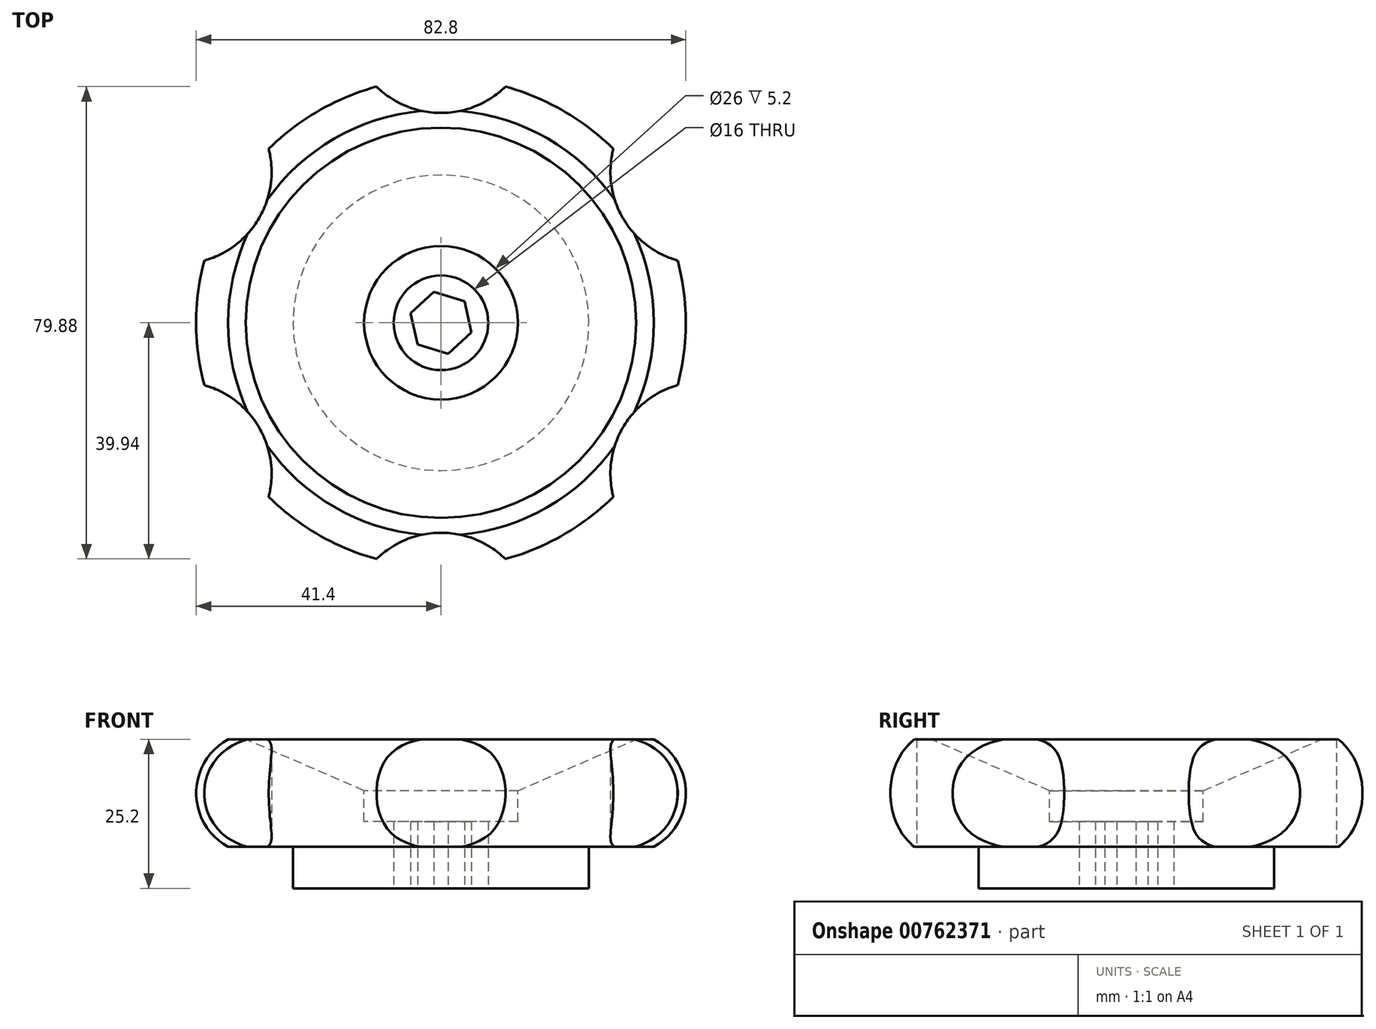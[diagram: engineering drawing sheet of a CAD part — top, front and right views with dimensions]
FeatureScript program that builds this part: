
annotation { "Feature Type Name" : "Feature", "Feature Type Description" : "" }
export const myFeature = defineFeature(function(context is Context, id is Id, definition is map)
    precondition{}
    {
        {
            var Q0;
            Q0=qCreatedBy(makeId("Front.planeOp"),FACE);
            var sketch = newSketch(context, id + "F0", { "sketchPlane" : qUnion([Q0])});
            skLineSegment(sketch, "E0", {"start": v(0, 0) * mm, "end": v(25, 0) * mm});
            skLineSegment(sketch, "E1", {"start": v(25, 0) * mm, "end": v(25, 7) * mm});
            skLineSegment(sketch, "E2", {"start": v(25, 7) * mm, "end": v(36, 7) * mm});
            skLineSegment(sketch, "E3.0", {"start": v(33, 25.2) * mm, "end": v(36, 25.2) * mm});
            skLineSegment(sketch, "E4.0", {"start": v(0, 11.3) * mm, "end": v(13, 11.3) * mm});
            skLineSegment(sketch, "E5", {"start": v(41.4, 60.5) * mm, "end": v(41.4, -63.46) * mm, "construction": true});
            skArc(sketch, "E6", {"start": v(36, 7) * mm, "mid": v(41.4, 16.1) * mm, "end": v(36, 25.2) * mm});
            skLineSegment(sketch, "E7", {"start": v(13, 11.3) * mm, "end": v(13, 16.5) * mm});
            skLineSegment(sketch, "E8", {"start": v(13, 16.5) * mm, "end": v(33, 25.2) * mm});
            skLineSegment(sketch, "E9", {"start": v(0, 11.3) * mm, "end": v(0, 0) * mm});
            skSolve(sketch);
        }
        {
            var Q0;
            Q0=makeQuery(id+"F0.imprint","IMPRINT",FACE,{"disambiguationData":[TD([[makeQuery(id+"F0.imprint","IMPRINT",EDGE,{"derivedFrom":sQuery(id+"F0.wireOp",EDGE,"E0")}),1.0]])]});
            var Q1;
            Q1=sQuery(id+"F0.wireOp",EDGE,"E9");
            revolve(context, id + "F1", {"surfaceOperationType" : NewSurfaceOperationType.NEW, "entities" : qUnion([Q0]), "axis" : qUnion([Q1]), "revolveType" : RevolveType.FULL});
        }
        {
            var Q0;
            Q0=makeQuery(id+"F1.opRevolve","SWEPT_FACE",FACE,{"disambiguationData":[OSD([sQuery(id+"F0.wireOp",EDGE,"E0")])]});
            var sketch = newSketch(context, id + "F2", { "sketchPlane" : qUnion([Q0])});
            skCircle(sketch, "E10", {"center": v(0, 0) * mm, "radius": 8 * mm});
            skLineSegment(sketch, "E11", {"start": v(0, -18.1) * mm, "end": v(0, 35.5) * mm, "construction": true});
            skPoint(sketch, "E12.orphan", {"position": v(-2.52, 3.63) * mm});
            skPoint(sketch, "E13.orphan", {"position": v(2.52, 3.63) * mm});
            skPoint(sketch, "E14.orphan", {"position": v(2.52, 11.78) * mm});
            skPoint(sketch, "E15.orphan", {"position": v(-2.52, 11.78) * mm});
            skLineSegment(sketch, "E16", {"start": v(-10.9, 48.35) * mm, "end": v(-10.9, 28.17) * mm});
            skLineSegment(sketch, "E17.MirrorCS", {"start": v(10.9, 48.35) * mm, "end": v(10.9, 28.17) * mm});
            skCircle(sketch, "E18", {"center": v(0, 0) * mm, "radius": 41.4 * mm, "construction": true});
            skCircle(sketch, "E19", {"center": v(0, 51.1) * mm, "radius": 15.6 * mm});
            skPoint(sketch, "E19.first.point", {"position": v(-10.9, 39.94) * mm});
            skPoint(sketch, "E19.first.point.positionSnap0", {"position": v(-10.9, 38.26) * mm});
            skPoint(sketch, "E19.second.point", {"position": v(10.9, 39.94) * mm});
            skCircle(sketch, "E20.1.0", {"center": v(-44.25, 25.55) * mm, "radius": 15.6 * mm});
            skCircle(sketch, "E20.2.0", {"center": v(-44.25, -25.55) * mm, "radius": 15.6 * mm});
            skCircle(sketch, "E20.3.0", {"center": v(0, -51.1) * mm, "radius": 15.6 * mm});
            skCircle(sketch, "E20.4.0", {"center": v(44.25, -25.55) * mm, "radius": 15.6 * mm});
            skCircle(sketch, "E20.5.0", {"center": v(44.25, 25.55) * mm, "radius": 15.6 * mm});
            skCircle(sketch, "E21.cCircle", {"center": v(0, 0) * mm, "radius": 4.67 * mm, "construction": true});
            skLineSegment(sketch, "E21.0", {"start": v(1.18, 5.26) * mm, "end": v(5.15, 1.6) * mm});
            skLineSegment(sketch, "E21.1", {"start": v(5.15, 1.6) * mm, "end": v(3.97, -3.66) * mm});
            skLineSegment(sketch, "E21.2", {"start": v(3.97, -3.66) * mm, "end": v(-1.18, -5.26) * mm});
            skLineSegment(sketch, "E21.3", {"start": v(-1.18, -5.26) * mm, "end": v(-5.15, -1.6) * mm});
            skLineSegment(sketch, "E21.4", {"start": v(-5.15, -1.6) * mm, "end": v(-3.97, 3.66) * mm});
            skLineSegment(sketch, "E21.5", {"start": v(-3.97, 3.66) * mm, "end": v(1.18, 5.26) * mm});
            skPoint(sketch, "E21.0.midPoint", {"position": v(3.17, 3.44) * mm});
            skSolve(sketch);
        }
        {
            var Q0;
            Q0=makeQuery(id+"F2.imprint","IMPRINT",FACE,{"disambiguationData":[TD([[makeQuery(id+"F2.imprint","IMPRINT",EDGE,{"derivedFrom":sQuery(id+"F2.wireOp",EDGE,"E19")}),1.0]])]});
            var Q1;
            Q1=makeQuery(id+"F2.imprint","IMPRINT",FACE,{"disambiguationData":[TD([[makeQuery(id+"F2.imprint","IMPRINT",EDGE,{"derivedFrom":sQuery(id+"F2.wireOp",EDGE,"E20.5.0")}),1.0]])]});
            var Q2;
            Q2=makeQuery(id+"F2.imprint","IMPRINT",FACE,{"disambiguationData":[TD([[makeQuery(id+"F2.imprint","IMPRINT",EDGE,{"derivedFrom":sQuery(id+"F2.wireOp",EDGE,"E20.4.0")}),1.0]])]});
            var Q3;
            Q3=makeQuery(id+"F2.imprint","IMPRINT",FACE,{"disambiguationData":[TD([[makeQuery(id+"F2.imprint","IMPRINT",EDGE,{"derivedFrom":sQuery(id+"F2.wireOp",EDGE,"E20.3.0")}),1.0]])]});
            var Q4;
            Q4=makeQuery(id+"F2.imprint","IMPRINT",FACE,{"disambiguationData":[TD([[makeQuery(id+"F2.imprint","IMPRINT",EDGE,{"derivedFrom":sQuery(id+"F2.wireOp",EDGE,"E20.2.0")}),1.0]])]});
            var Q5;
            Q5=makeQuery(id+"F2.imprint","IMPRINT",FACE,{"disambiguationData":[TD([[makeQuery(id+"F2.imprint","IMPRINT",EDGE,{"derivedFrom":sQuery(id+"F2.wireOp",EDGE,"E20.1.0")}),1.0]])]});
            var Q6;
            {var subQ0=sQuery(id+"F2.wireOp",EDGE,"E10");var subQ1=makeQuery(id+"F2.imprint","INTERSECT",VERTEX,{"derivedFrom":[subQ0,sQuery(id+"F2.wireOp",EDGE,"E64xBf1T-4pr8-hSRn-79ht-nJzzQliX75lc")]});Q6=makeQuery(id+"F2.imprint","IMPRINT",FACE,{"disambiguationData":[TD([[makeQuery(id+"F2.imprint","IMPRINT",EDGE,{"disambiguationData":[TD([[subQ1,1.0]])],"derivedFrom":subQ0}),1.0]])]});}
            var Q7;
            Q7=makeQuery(id+"F2.imprint","IMPRINT",FACE,{"disambiguationData":[TD([[makeQuery(id+"F2.imprint","IMPRINT",EDGE,{"derivedFrom":sQuery(id+"F2.wireOp",EDGE,"FQK9e2zu-M0aR-wMkr-MjfM-o39hJ4Gc2hOX")}),-1.0]])]});
            extrude(context, id + "F3", {"entities" : qUnion([Q0, Q1, Q2, Q3, Q4, Q5, Q6, Q7]), "operationType" : NewBodyOperationType.REMOVE, "endBound" : BoundingType.THROUGH_ALL, "oppositeDirection" : true, "depth" : 25 * mm, "offsetDistance" : 25 * mm});
        }
        {
            var Q0;
            Q0=makeQuery(id+"F2.imprint","IMPRINT",FACE,{"disambiguationData":[TD([[makeQuery(id+"F2.imprint","IMPRINT",EDGE,{"derivedFrom":sQuery(id+"F2.wireOp",EDGE,"E10")}),1.0]])]});
            var Q1;
            Q1=sQuery(id+"F2.wireOp",EDGE,"E21.3");
            var Q2;
            Q2=sQuery(id+"F2.wireOp",EDGE,"E21.2");
            var Q3;
            Q3=sQuery(id+"F2.wireOp",EDGE,"E21.4");
            var Q4;
            Q4=sQuery(id+"F2.wireOp",EDGE,"E21.5");
            var Q5;
            Q5=sQuery(id+"F2.wireOp",EDGE,"E21.0");
            var Q6;
            Q6=sQuery(id+"F2.wireOp",EDGE,"E21.1");
            extrude(context, id + "F4", {"entities" : qUnion([Q0]), "operationType" : NewBodyOperationType.REMOVE, "surfaceEntities" : qUnion([Q1, Q2, Q3, Q4, Q5, Q6]), "endBound" : BoundingType.SYMMETRIC, "oppositeDirection" : true, "depth" : 25.2 * mm, "hasOffset" : true, "offsetDistance" : 25 * mm});
        }
    });
